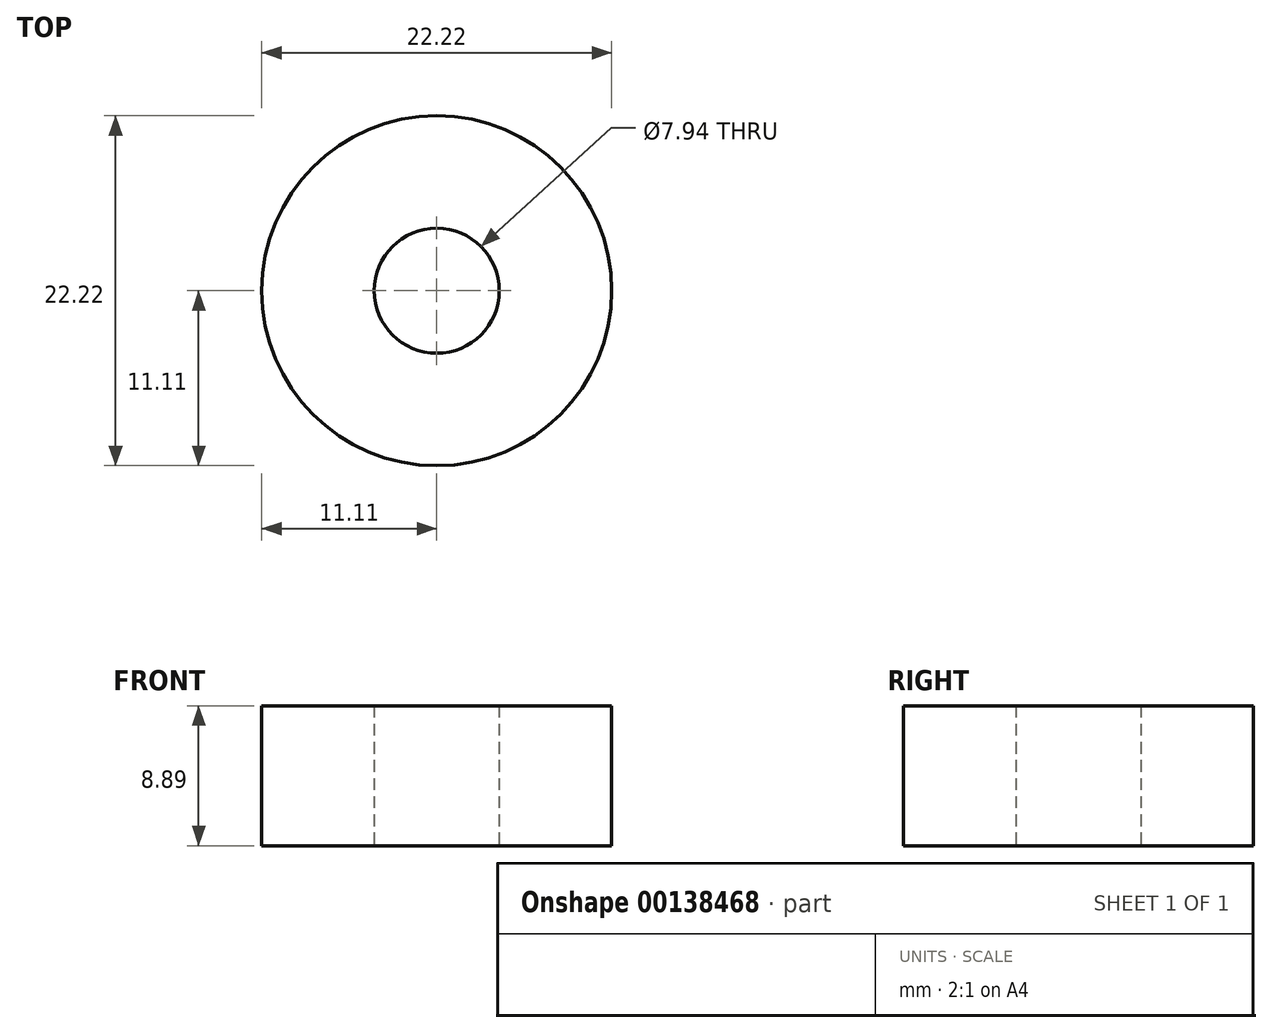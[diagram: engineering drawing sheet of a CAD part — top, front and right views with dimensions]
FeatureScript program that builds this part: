
annotation { "Feature Type Name" : "Feature", "Feature Type Description" : "" }
export const myFeature = defineFeature(function(context is Context, id is Id, definition is map)
    precondition{}
    {
        {
            var Q0;
            Q0=qCreatedBy(makeId("Top.planeOp"),FACE);
            var sketch = newSketch(context, id + "F0", { "sketchPlane" : qUnion([Q0])});
            skCircle(sketch, "E0", {"center": v(0, 0) * mm, "radius": 11.11 * mm});
            skCircle(sketch, "E1", {"center": v(0, 0) * mm, "radius": 3.97 * mm});
            skSolve(sketch);
        }
        {
            var Q0;
            Q0 = qSketchRegion(id + "F0", true);
            extrude(context, id + "F1", {"entities" : qUnion([Q0]), "depth" : 8.9 * mm});
        }
    });
